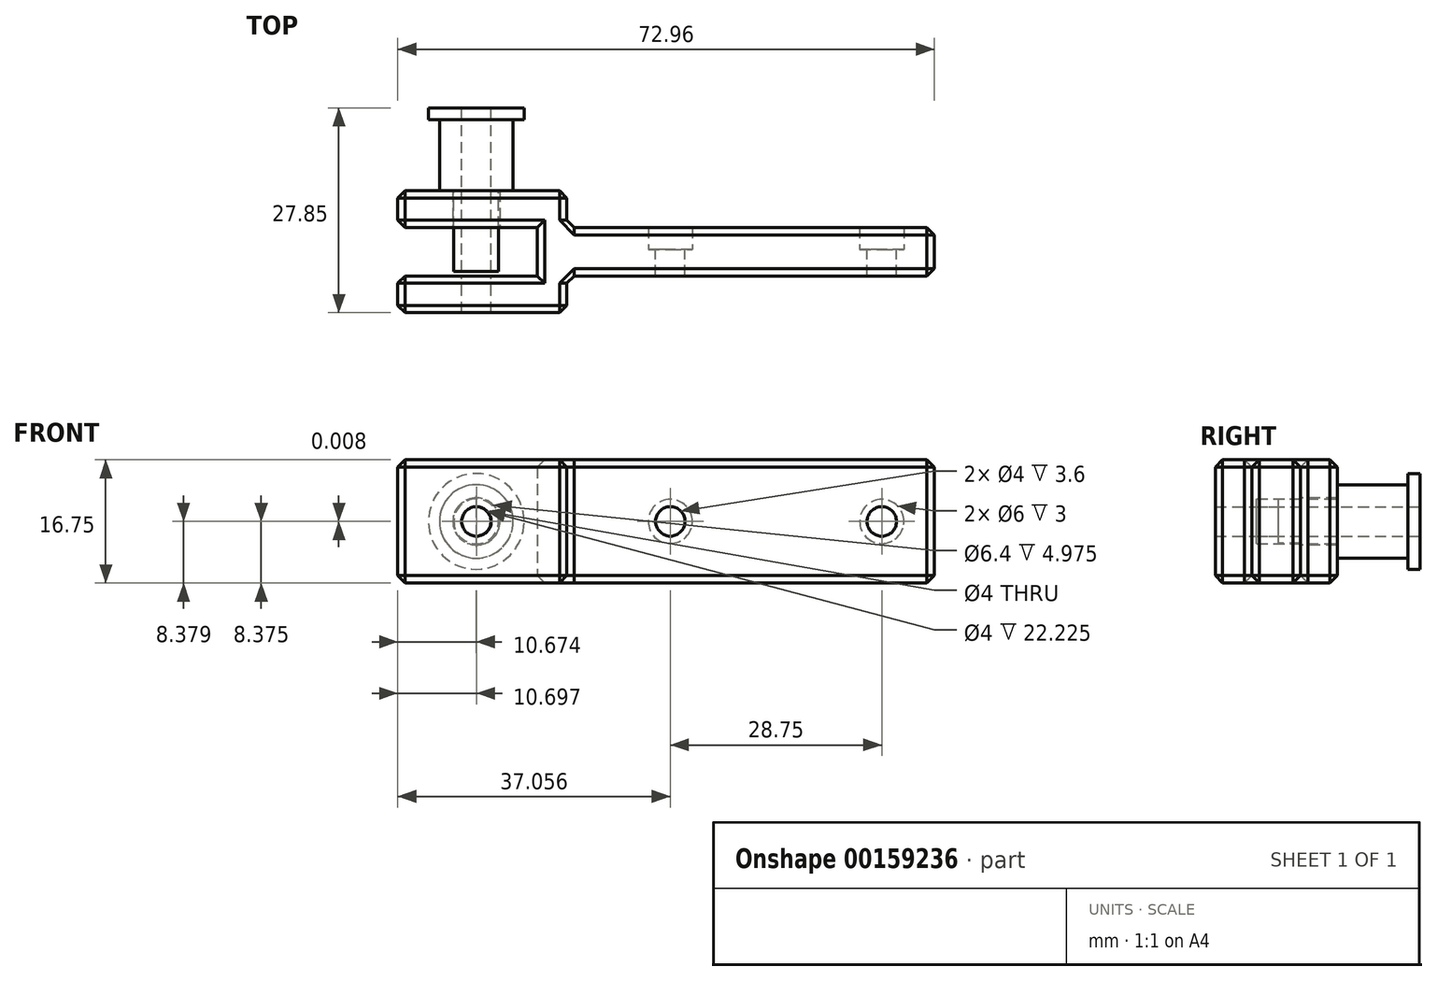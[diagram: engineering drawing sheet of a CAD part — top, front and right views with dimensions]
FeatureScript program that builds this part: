
annotation { "Feature Type Name" : "Feature", "Feature Type Description" : "" }
export const myFeature = defineFeature(function(context is Context, id is Id, definition is map)
    precondition{}
    {
        {
            var Q0;
            Q0=qCreatedBy(makeId("Top.planeOp"),FACE);
            var sketch = newSketch(context, id + "F0", { "sketchPlane" : qUnion([Q0])});
            skLineSegment(sketch, "E0.bottom", {"start": v(-43.93, 8.3) * mm, "end": v(-20.93, 8.3) * mm});
            skLineSegment(sketch, "E0.right", {"start": v(-20.93, 8.3) * mm, "end": v(-20.93, 0) * mm});
            skLineSegment(sketch, "E1.bottom", {"start": v(-20.97, 3.3) * mm, "end": v(29.03, 3.3) * mm});
            skLineSegment(sketch, "E1.right", {"start": v(29.03, 3.3) * mm, "end": v(29.03, 0) * mm});
            skLineSegment(sketch, "E2", {"start": v(-44.8, 0) * mm, "end": v(49.31, 0) * mm, "construction": true});
            skLineSegment(sketch, "E3", {"start": v(-43.93, 3.3) * mm, "end": v(-24.93, 3.3) * mm});
            skLineSegment(sketch, "E4", {"start": v(-24.93, 3.3) * mm, "end": v(-24.93, 0) * mm});
            skLineSegment(sketch, "E5", {"start": v(-43.93, 8.3) * mm, "end": v(-43.93, 3.3) * mm});
            skLineSegment(sketch, "E6.MirrorCS", {"start": v(-43.93, -8.3) * mm, "end": v(-43.93, -3.3) * mm});
            skLineSegment(sketch, "E7.MirrorCS", {"start": v(-20.93, -8.3) * mm, "end": v(-20.93, 0) * mm});
            skLineSegment(sketch, "E8.MirrorCS", {"start": v(29.03, -3.3) * mm, "end": v(29.03, 0) * mm});
            skLineSegment(sketch, "E9.MirrorCS", {"start": v(-24.93, -3.3) * mm, "end": v(-24.93, 0) * mm});
            skLineSegment(sketch, "E10.MirrorCS", {"start": v(-43.93, -3.3) * mm, "end": v(-24.93, -3.3) * mm});
            skLineSegment(sketch, "E11.MirrorCS", {"start": v(-20.97, -3.3) * mm, "end": v(29.03, -3.3) * mm});
            skLineSegment(sketch, "E12.MirrorCS", {"start": v(-43.93, -8.3) * mm, "end": v(-20.93, -8.3) * mm});
            skSolve(sketch);
        }
        {
            var Q0;
            {var subQ4=sQuery(id+"F0.wireOp",EDGE,"E0.bottom");Q0=makeQuery(id+"F0.imprint","IMPRINT",FACE,{"disambiguationData":[TD([[makeQuery(id+"F0.imprint","IMPRINT",EDGE,{"derivedFrom":subQ4}),-1.0]])]});}
            var Q1;
            {var subQ5=sQuery(id+"F0.wireOp",EDGE,"E1.right");Q1=makeQuery(id+"F0.imprint","IMPRINT",FACE,{"disambiguationData":[TD([[makeQuery(id+"F0.imprint","IMPRINT",EDGE,{"derivedFrom":subQ5}),-1.0]])]});}
            extrude(context, id + "F1", {"entities" : qUnion([Q0, Q1]), "depth" : 16.75 * mm});
        }
        {
            var Q0;
            Q0=qCreatedBy(makeId("Front.planeOp"),FACE);
            var sketch = newSketch(context, id + "F2", { "sketchPlane" : qUnion([Q0])});
            skLineSegment(sketch, "E13", {"start": v(-52.03, 8.38) * mm, "end": v(37.95, 8.38) * mm, "construction": true});
            skCircle(sketch, "E14", {"center": v(21.88, 8.38) * mm, "radius": 2 * mm});
            skCircle(sketch, "E15", {"center": v(-6.87, 8.38) * mm, "radius": 2 * mm});
            skCircle(sketch, "E16", {"center": v(-33.23, 8.38) * mm, "radius": 3.2 * mm});
            skCircle(sketch, "E17", {"center": v(-33.23, 8.38) * mm, "radius": 2 * mm});
            skLineSegment(sketch, "E18", {"start": v(-33.23, 8.38) * mm, "end": v(-33.23, 14.41) * mm, "construction": true});
            skLineSegment(sketch, "E19", {"start": v(-33.23, 14.41) * mm, "end": v(-33.23, 8.38) * mm, "construction": true});
            skLineSegment(sketch, "E20", {"start": v(-33.23, 8.38) * mm, "end": v(-33.23, 1.83) * mm, "construction": true});
            skCircle(sketch, "E21", {"center": v(-6.87, 8.38) * mm, "radius": 3 * mm});
            skCircle(sketch, "E22", {"center": v(21.88, 8.38) * mm, "radius": 3 * mm});
            skSolve(sketch);
        }
        {
            var Q0;
            Q0=makeQuery(id+"F2.imprint","IMPRINT",FACE,{"disambiguationData":[TD([[makeQuery(id+"F2.imprint","IMPRINT",EDGE,{"derivedFrom":sQuery(id+"F2.wireOp",EDGE,"E14")}),1.0]])]});
            var Q1;
            Q1=makeQuery(id+"F2.imprint","IMPRINT",FACE,{"disambiguationData":[TD([[makeQuery(id+"F2.imprint","IMPRINT",EDGE,{"derivedFrom":sQuery(id+"F2.wireOp",EDGE,"E15")}),1.0]])]});
            extrude(context, id + "F3", {"entities" : qUnion([Q0, Q1]), "operationType" : NewBodyOperationType.REMOVE, "endBound" : BoundingType.SYMMETRIC, "depth" : 25 * mm});
        }
        {
            var Q0;
            Q0=makeQuery(id+"F1.opExtrude","CAP_EDGE",EDGE,{"disambiguationData":[OSD([sQuery(id+"F0.wireOp",EDGE,"E12.MirrorCS")])],"isStart":false});
            var Q1;
            Q1=makeQuery(id+"F1.opExtrude","CAP_EDGE",EDGE,{"disambiguationData":[OSD([sQuery(id+"F0.wireOp",EDGE,"E7.MirrorCS")])],"isStart":false});
            var Q2;
            Q2=makeQuery(id+"F1.opExtrude","CAP_EDGE",EDGE,{"disambiguationData":[OSD([sQuery(id+"F0.wireOp",EDGE,"E11.MirrorCS")])],"isStart":false});
            var Q3;
            Q3=makeQuery(id+"F1.opExtrude","CAP_EDGE",EDGE,{"disambiguationData":[OSD([sQuery(id+"F0.wireOp",EDGE,"E1.right"),sQuery(id+"F0.wireOp",EDGE,"E8.MirrorCS")])],"isStart":false});
            var Q4;
            Q4=makeQuery(id+"F1.opExtrude","CAP_EDGE",EDGE,{"disambiguationData":[OSD([sQuery(id+"F0.wireOp",EDGE,"E1.bottom")])],"isStart":false});
            var Q5;
            Q5=makeQuery(id+"F1.opExtrude","CAP_EDGE",EDGE,{"disambiguationData":[OSD([sQuery(id+"F0.wireOp",EDGE,"E0.right")])],"isStart":false});
            var Q6;
            Q6=makeQuery(id+"F1.opExtrude","CAP_EDGE",EDGE,{"disambiguationData":[OSD([sQuery(id+"F0.wireOp",EDGE,"E0.bottom")])],"isStart":false});
            var Q7;
            Q7=makeQuery(id+"F1.opExtrude","CAP_EDGE",EDGE,{"disambiguationData":[OSD([sQuery(id+"F0.wireOp",EDGE,"E5")])],"isStart":false});
            var Q8;
            Q8=makeQuery(id+"F1.opExtrude","CAP_EDGE",EDGE,{"disambiguationData":[OSD([sQuery(id+"F0.wireOp",EDGE,"E6.MirrorCS")])],"isStart":false});
            var Q9;
            Q9=makeQuery(id+"F1.opExtrude","SWEPT_EDGE",EDGE,{"disambiguationData":[OSD([sQuery(id+"F0.wireOp",EDGE,"E8.MirrorCS"),sQuery(id+"F0.wireOp",EDGE,"E11.MirrorCS")])]});
            var Q10;
            Q10=makeQuery(id+"F1.opExtrude","SWEPT_EDGE",EDGE,{"disambiguationData":[OSD([sQuery(id+"F0.wireOp",EDGE,"E1.bottom"),sQuery(id+"F0.wireOp",EDGE,"E1.right")])]});
            var Q11;
            Q11=makeQuery(id+"F1.opExtrude","CAP_EDGE",EDGE,{"disambiguationData":[OSD([sQuery(id+"F0.wireOp",EDGE,"E1.bottom")])],"isStart":true});
            var Q12;
            Q12=makeQuery(id+"F1.opExtrude","CAP_EDGE",EDGE,{"disambiguationData":[OSD([sQuery(id+"F0.wireOp",EDGE,"E11.MirrorCS")])],"isStart":true});
            var Q13;
            Q13=makeQuery(id+"F1.opExtrude","CAP_EDGE",EDGE,{"disambiguationData":[OSD([sQuery(id+"F0.wireOp",EDGE,"E7.MirrorCS")])],"isStart":true});
            var Q14;
            Q14=makeQuery(id+"F1.opExtrude","CAP_EDGE",EDGE,{"disambiguationData":[OSD([sQuery(id+"F0.wireOp",EDGE,"E0.right")])],"isStart":true});
            var Q15;
            Q15=makeQuery(id+"F1.opExtrude","SWEPT_EDGE",EDGE,{"disambiguationData":[OSD([sQuery(id+"F0.wireOp",EDGE,"E7.MirrorCS"),sQuery(id+"F0.wireOp",EDGE,"E12.MirrorCS")])]});
            var Q16;
            Q16=makeQuery(id+"F1.opExtrude","SWEPT_EDGE",EDGE,{"disambiguationData":[OSD([sQuery(id+"F0.wireOp",EDGE,"E0.bottom"),sQuery(id+"F0.wireOp",EDGE,"E0.right")])]});
            var Q17;
            Q17=makeQuery(id+"F1.opExtrude","CAP_EDGE",EDGE,{"disambiguationData":[OSD([sQuery(id+"F0.wireOp",EDGE,"E0.bottom")])],"isStart":true});
            var Q18;
            Q18=makeQuery(id+"F1.opExtrude","CAP_EDGE",EDGE,{"disambiguationData":[OSD([sQuery(id+"F0.wireOp",EDGE,"E12.MirrorCS")])],"isStart":true});
            var Q19;
            Q19=makeQuery(id+"F1.opExtrude","CAP_EDGE",EDGE,{"disambiguationData":[OSD([sQuery(id+"F0.wireOp",EDGE,"E4"),sQuery(id+"F0.wireOp",EDGE,"E9.MirrorCS")])],"isStart":true});
            var Q20;
            Q20=makeQuery(id+"F1.opExtrude","CAP_EDGE",EDGE,{"disambiguationData":[OSD([sQuery(id+"F0.wireOp",EDGE,"E4"),sQuery(id+"F0.wireOp",EDGE,"E9.MirrorCS")])],"isStart":false});
            var Q21;
            Q21=makeQuery(id+"F1.opExtrude","CAP_EDGE",EDGE,{"disambiguationData":[OSD([sQuery(id+"F0.wireOp",EDGE,"E3")])],"isStart":false});
            var Q22;
            Q22=makeQuery(id+"F1.opExtrude","CAP_EDGE",EDGE,{"disambiguationData":[OSD([sQuery(id+"F0.wireOp",EDGE,"E10.MirrorCS")])],"isStart":false});
            var Q23;
            Q23=makeQuery(id+"F1.opExtrude","CAP_EDGE",EDGE,{"disambiguationData":[OSD([sQuery(id+"F0.wireOp",EDGE,"E10.MirrorCS")])],"isStart":true});
            var Q24;
            Q24=makeQuery(id+"F1.opExtrude","CAP_EDGE",EDGE,{"disambiguationData":[OSD([sQuery(id+"F0.wireOp",EDGE,"E3")])],"isStart":true});
            var Q25;
            Q25=makeQuery(id+"F1.opExtrude","SWEPT_EDGE",EDGE,{"disambiguationData":[OSD([sQuery(id+"F0.wireOp",EDGE,"E6.MirrorCS"),sQuery(id+"F0.wireOp",EDGE,"E12.MirrorCS")])]});
            var Q26;
            Q26=makeQuery(id+"F1.opExtrude","SWEPT_EDGE",EDGE,{"disambiguationData":[OSD([sQuery(id+"F0.wireOp",EDGE,"E0.bottom"),sQuery(id+"F0.wireOp",EDGE,"E5")])]});
            var Q27;
            Q27=makeQuery(id+"F1.opExtrude","SWEPT_EDGE",EDGE,{"disambiguationData":[OSD([sQuery(id+"F0.wireOp",EDGE,"E3"),sQuery(id+"F0.wireOp",EDGE,"E5")])]});
            var Q28;
            Q28=makeQuery(id+"F1.opExtrude","SWEPT_EDGE",EDGE,{"disambiguationData":[OSD([sQuery(id+"F0.wireOp",EDGE,"E6.MirrorCS"),sQuery(id+"F0.wireOp",EDGE,"E10.MirrorCS")])]});
            var Q29;
            Q29=makeQuery(id+"F1.opExtrude","CAP_EDGE",EDGE,{"disambiguationData":[OSD([sQuery(id+"F0.wireOp",EDGE,"E5")])],"isStart":true});
            var Q30;
            Q30=makeQuery(id+"F1.opExtrude","CAP_EDGE",EDGE,{"disambiguationData":[OSD([sQuery(id+"F0.wireOp",EDGE,"E6.MirrorCS")])],"isStart":true});
            var Q31;
            Q31=makeQuery(id+"F1.opExtrude","CAP_EDGE",EDGE,{"disambiguationData":[OSD([sQuery(id+"F0.wireOp",EDGE,"E1.right"),sQuery(id+"F0.wireOp",EDGE,"E8.MirrorCS")])],"isStart":true});
            var Q32;
            Q32=makeQuery(id+"F1.opExtrude","SWEPT_EDGE",EDGE,{"disambiguationData":[OSD([sQuery(id+"F0.wireOp",EDGE,"E7.MirrorCS"),sQuery(id+"F0.wireOp",EDGE,"E11.MirrorCS")])]});
            var Q33;
            Q33=makeQuery(id+"F1.opExtrude","SWEPT_EDGE",EDGE,{"disambiguationData":[OSD([sQuery(id+"F0.wireOp",EDGE,"E0.right"),sQuery(id+"F0.wireOp",EDGE,"E1.bottom")])]});
            chamfer(context, id + "F4", {"entities" : qUnion([Q0, Q1, Q2, Q3, Q4, Q5, Q6, Q7, Q8, Q9, Q10, Q11, Q12, Q13, Q14, Q15, Q16, Q17, Q18, Q19, Q20, Q21, Q22, Q23, Q24, Q25, Q26, Q27, Q28, Q29, Q30, Q31, Q32, Q33]), "width" : 1 * mm, "tangentPropagation" : true});
        }
        {
            var Q0;
            Q0=makeQuery(id+"F2.imprint","IMPRINT",FACE,{"disambiguationData":[TD([[makeQuery(id+"F2.imprint","IMPRINT",EDGE,{"derivedFrom":sQuery(id+"F2.wireOp",EDGE,"E16")}),1.0]])]});
            var Q1;
            Q1=makeQuery(id+"F2.imprint","IMPRINT",FACE,{"disambiguationData":[TD([[makeQuery(id+"F2.imprint","IMPRINT",EDGE,{"derivedFrom":sQuery(id+"F2.wireOp",EDGE,"E17")}),1.0]])]});
            extrude(context, id + "F5", {"entities" : qUnion([Q0, Q1]), "operationType" : NewBodyOperationType.REMOVE, "oppositeDirection" : true, "depth" : 25 * mm});
        }
        {
            var Q0;
            Q0=makeQuery(id+"F2.imprint","IMPRINT",FACE,{"disambiguationData":[TD([[makeQuery(id+"F2.imprint","IMPRINT",EDGE,{"derivedFrom":sQuery(id+"F2.wireOp",EDGE,"E17")}),1.0]])]});
            extrude(context, id + "F6", {"entities" : qUnion([Q0]), "operationType" : NewBodyOperationType.REMOVE, "depth" : 15.55 * mm});
        }
        {
            var Q0;
            Q0=qCreatedBy(makeId("Front.planeOp"),FACE);
            var sketch = newSketch(context, id + "F7", { "sketchPlane" : qUnion([Q0])});
            skLineSegment(sketch, "E23", {"start": v(-41.57, 8.38) * mm, "end": v(-27.87, 8.38) * mm, "construction": true});
            skLineSegment(sketch, "E24", {"start": v(-33.26, 8.38) * mm, "end": v(-33.26, 14.43) * mm, "construction": true});
            skLineSegment(sketch, "E25", {"start": v(-33.26, 14.43) * mm, "end": v(-33.26, 3.62) * mm, "construction": true});
            skCircle(sketch, "E26", {"center": v(-33.26, 8.38) * mm, "radius": 2 * mm});
            skCircle(sketch, "E27", {"center": v(-33.26, 8.38) * mm, "radius": 3.05 * mm});
            skCircle(sketch, "E28", {"center": v(-33.26, 8.38) * mm, "radius": 5 * mm});
            skCircle(sketch, "E29", {"center": v(-33.26, 8.38) * mm, "radius": 6.5 * mm});
            skSolve(sketch);
        }
        {
            var Q0;
            Q0=makeQuery(id+"F7.imprint","IMPRINT",FACE,{"disambiguationData":[TD([[makeQuery(id+"F7.imprint","IMPRINT",EDGE,{"derivedFrom":sQuery(id+"F7.wireOp",EDGE,"E26")}),-1.0]])]});
            extrude(context, id + "F8", {"entities" : qUnion([Q0]), "depth" : 2.67 * mm, "hasSecondDirection" : true, "secondDirectionOppositeDirection" : true, "secondDirectionDepth" : 18 * mm});
        }
        {
            var Q0;
            Q0=makeQuery(id+"F7.imprint","IMPRINT",FACE,{"disambiguationData":[TD([[makeQuery(id+"F7.imprint","IMPRINT",EDGE,{"derivedFrom":sQuery(id+"F7.wireOp",EDGE,"E27")}),-1.0]])]});
            extrude(context, id + "F9", {"entities" : qUnion([Q0]), "operationType" : NewBodyOperationType.ADD, "oppositeDirection" : true, "depth" : 18 * mm, "hasSecondDirection" : true, "secondDirectionOppositeDirection" : true, "secondDirectionDepth" : 8.27 * mm});
        }
        {
            var Q0;
            Q0=makeQuery(id+"F2.imprint","IMPRINT",FACE,{"disambiguationData":[TD([[makeQuery(id+"F2.imprint","IMPRINT",EDGE,{"derivedFrom":sQuery(id+"F2.wireOp",EDGE,"E14")}),-1.0]])]});
            var Q1;
            Q1=makeQuery(id+"F2.imprint","IMPRINT",FACE,{"disambiguationData":[TD([[makeQuery(id+"F2.imprint","IMPRINT",EDGE,{"derivedFrom":sQuery(id+"F2.wireOp",EDGE,"E15")}),-1.0]])]});
            extrude(context, id + "F10", {"entities" : qUnion([Q0, Q1]), "operationType" : NewBodyOperationType.REMOVE, "oppositeDirection" : true, "depth" : 10.15 * mm, "hasSecondDirection" : true, "secondDirectionOppositeDirection" : true, "secondDirectionDepth" : 0.3 * mm});
        }
        {
            var Q0;
            Q0=makeQuery(id+"F7.imprint","IMPRINT",FACE,{"disambiguationData":[TD([[makeQuery(id+"F7.imprint","IMPRINT",EDGE,{"derivedFrom":sQuery(id+"F7.wireOp",EDGE,"E28")}),-1.0]])]});
            var Q1;
            Q1=makeQuery(id+"F7.imprint","IMPRINT",FACE,{"disambiguationData":[TD([[makeQuery(id+"F7.imprint","IMPRINT",EDGE,{"derivedFrom":sQuery(id+"F7.wireOp",EDGE,"E27")}),-1.0]])]});
            var Q2;
            Q2=makeQuery(id+"F7.imprint","IMPRINT",FACE,{"disambiguationData":[TD([[makeQuery(id+"F7.imprint","IMPRINT",EDGE,{"derivedFrom":sQuery(id+"F7.wireOp",EDGE,"E26")}),-1.0]])]});
            extrude(context, id + "F11", {"entities" : qUnion([Q0, Q1, Q2]), "operationType" : NewBodyOperationType.ADD, "oppositeDirection" : true, "depth" : 19.55 * mm, "hasSecondDirection" : true, "secondDirectionOppositeDirection" : true, "secondDirectionDepth" : 17.93 * mm});
        }
    });
